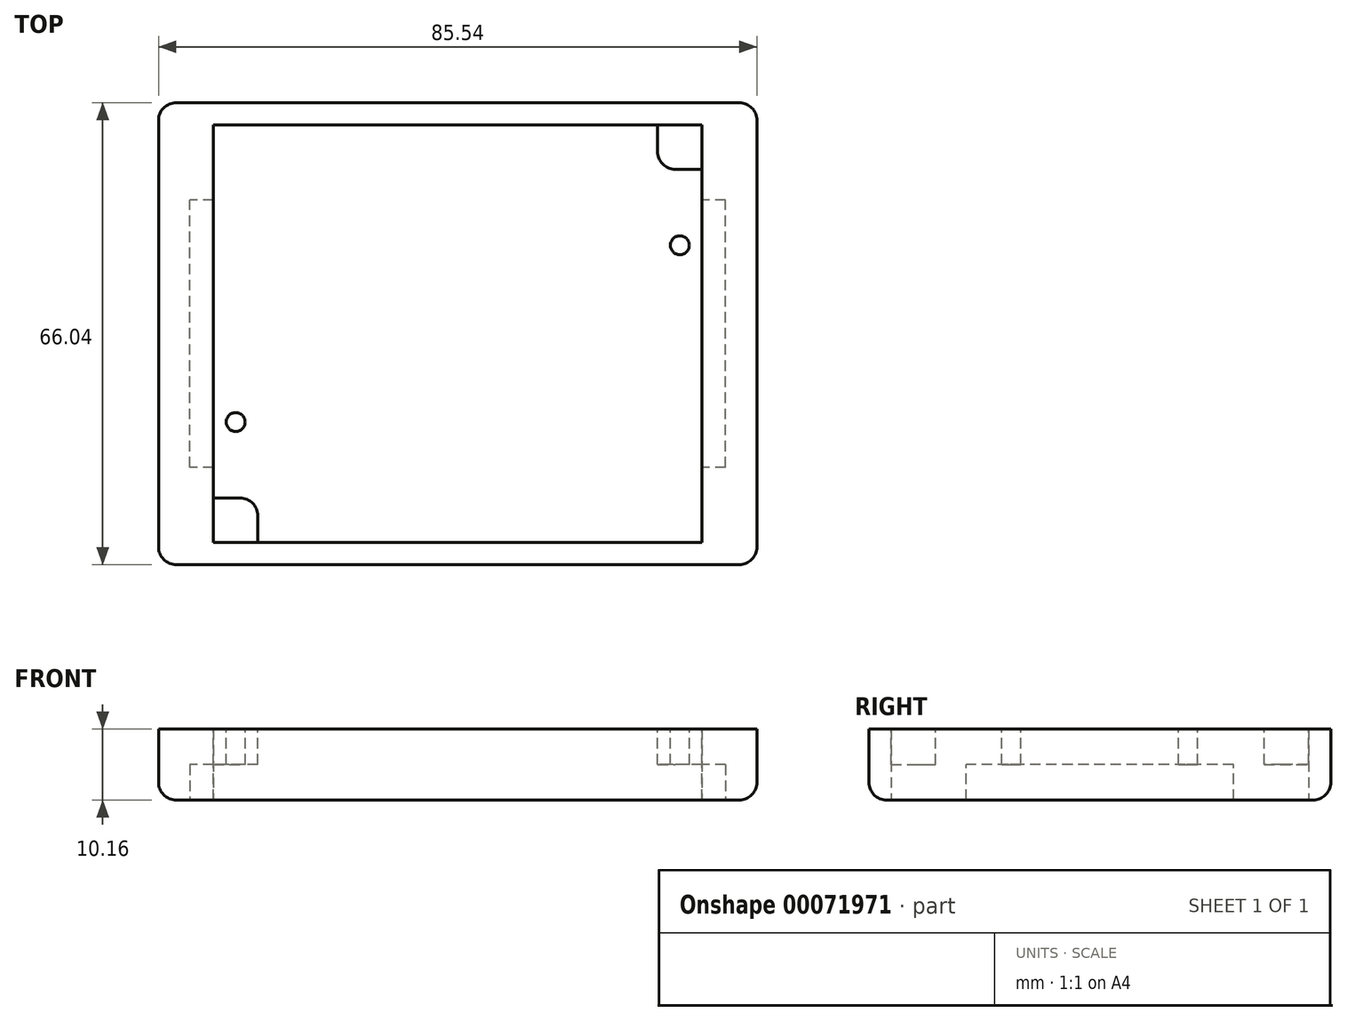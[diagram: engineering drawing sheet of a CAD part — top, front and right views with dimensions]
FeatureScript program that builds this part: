
annotation { "Feature Type Name" : "Feature", "Feature Type Description" : "" }
export const myFeature = defineFeature(function(context is Context, id is Id, definition is map)
    precondition{}
    {
        {
            var Q0;
            Q0=qCreatedBy(makeId("Top.planeOp"),FACE);
            var sketch = newSketch(context, id + "F0", { "sketchPlane" : qUnion([Q0])});
            skLineSegment(sketch, "E0.rect.bottom", {"start": v(34.92, -29.85) * mm, "end": v(-34.93, -29.85) * mm});
            skLineSegment(sketch, "E0.rect.top", {"start": v(34.92, 29.85) * mm, "end": v(-34.93, 29.85) * mm});
            skLineSegment(sketch, "E0.rect.left", {"start": v(34.92, -29.85) * mm, "end": v(34.92, 29.85) * mm});
            skLineSegment(sketch, "E0.rect.right", {"start": v(-34.93, -29.85) * mm, "end": v(-34.93, 29.85) * mm});
            skPoint(sketch, "E0.rect.middle", {"position": v(0, 0) * mm});
            skLineSegment(sketch, "E1.rect.bottom", {"start": v(42.77, -33.02) * mm, "end": v(-42.77, -33.02) * mm});
            skLineSegment(sketch, "E1.rect.top", {"start": v(42.77, 33.02) * mm, "end": v(-42.77, 33.02) * mm});
            skLineSegment(sketch, "E1.rect.left", {"start": v(42.77, -33.02) * mm, "end": v(42.77, 33.02) * mm});
            skLineSegment(sketch, "E1.rect.right", {"start": v(-42.77, -33.02) * mm, "end": v(-42.77, 33.02) * mm});
            skSolve(sketch);
        }
        {
            var Q0;
            Q0=makeQuery(id+"F0.imprint","IMPRINT",FACE,{"disambiguationData":[TD([[makeQuery(id+"F0.imprint","IMPRINT",EDGE,{"derivedFrom":sQuery(id+"F0.wireOp",EDGE,"E0.rect.bottom")}),1.0]])]});
            extrude(context, id + "F1", {"entities" : qUnion([Q0]), "depth" : 10.16 * mm});
        }
        {
            var Q0;
            Q0=makeQuery(id+"F1.opExtrude","CAP_FACE",FACE,{"disambiguationData":[OSD([sQuery(id+"F0.wireOp",EDGE,"E0.rect.bottom"),sQuery(id+"F0.wireOp",EDGE,"E0.rect.top"),sQuery(id+"F0.wireOp",EDGE,"E0.rect.left"),sQuery(id+"F0.wireOp",EDGE,"E0.rect.right"),sQuery(id+"F0.wireOp",EDGE,"E1.rect.bottom"),sQuery(id+"F0.wireOp",EDGE,"E1.rect.top"),sQuery(id+"F0.wireOp",EDGE,"E1.rect.left"),sQuery(id+"F0.wireOp",EDGE,"E1.rect.right")])],"isStart":false});
            var sketch = newSketch(context, id + "F2", { "sketchPlane" : qUnion([Q0])});
            skLineSegment(sketch, "E2.bottom", {"start": v(-34.93, -29.85) * mm, "end": v(-28.57, -29.85) * mm});
            skLineSegment(sketch, "E2.top", {"start": v(-34.93, -23.5) * mm, "end": v(-28.57, -23.5) * mm});
            skLineSegment(sketch, "E2.left", {"start": v(-34.93, -29.85) * mm, "end": v(-34.93, -23.5) * mm});
            skLineSegment(sketch, "E2.right", {"start": v(-28.57, -29.85) * mm, "end": v(-28.57, -23.5) * mm});
            skLineSegment(sketch, "E3.bottom", {"start": v(34.92, 29.85) * mm, "end": v(28.57, 29.85) * mm});
            skLineSegment(sketch, "E3.top", {"start": v(34.92, 23.5) * mm, "end": v(28.57, 23.5) * mm});
            skLineSegment(sketch, "E3.left", {"start": v(34.92, 29.85) * mm, "end": v(34.92, 23.5) * mm});
            skLineSegment(sketch, "E3.right", {"start": v(28.57, 29.85) * mm, "end": v(28.57, 23.5) * mm});
            skCircle(sketch, "E4", {"center": v(-31.75, -12.64) * mm, "radius": 1.35 * mm});
            skCircle(sketch, "E5", {"center": v(31.75, 12.64) * mm, "radius": 1.35 * mm});
            skSolve(sketch);
        }
        {
            var Q0;
            Q0 = qSketchRegion(id + "F2", true);
            extrude(context, id + "F3", {"entities" : qUnion([Q0]), "oppositeDirection" : true, "depth" : 5.08 * mm});
        }
        {
            var Q0;
            Q0=makeQuery(id+"F3.opExtrude","SWEPT_EDGE",EDGE,{"disambiguationData":[OSD([sQuery(id+"F2.wireOp",EDGE,"E3.top"),sQuery(id+"F2.wireOp",EDGE,"E3.right")])]});
            var Q1;
            Q1=makeQuery(id+"F3.opExtrude","SWEPT_EDGE",EDGE,{"disambiguationData":[OSD([sQuery(id+"F2.wireOp",EDGE,"E2.top"),sQuery(id+"F2.wireOp",EDGE,"E2.right")])]});
            fillet(context, id + "F4", {"entities" : qUnion([Q0, Q1]), "radius" : 2.54 * mm, "tangentPropagation" : true, "allowEdgeOverflow" : false});
        }
        {
            var Q0;
            Q0=makeQuery(id+"F1.opExtrude","CAP_FACE",FACE,{"disambiguationData":[OSD([sQuery(id+"F0.wireOp",EDGE,"E0.rect.bottom"),sQuery(id+"F0.wireOp",EDGE,"E0.rect.top"),sQuery(id+"F0.wireOp",EDGE,"E0.rect.left"),sQuery(id+"F0.wireOp",EDGE,"E0.rect.right"),sQuery(id+"F0.wireOp",EDGE,"E1.rect.bottom"),sQuery(id+"F0.wireOp",EDGE,"E1.rect.top"),sQuery(id+"F0.wireOp",EDGE,"E1.rect.left"),sQuery(id+"F0.wireOp",EDGE,"E1.rect.right")])],"isStart":true});
            var sketch = newSketch(context, id + "F5", { "sketchPlane" : qUnion([Q0])});
            skLineSegment(sketch, "E6.rect.bottom", {"start": v(38.3, 19.11) * mm, "end": v(-38.3, 19.11) * mm});
            skLineSegment(sketch, "E6.rect.top", {"start": v(38.3, -19.11) * mm, "end": v(-38.3, -19.11) * mm});
            skLineSegment(sketch, "E6.rect.left", {"start": v(38.3, 19.11) * mm, "end": v(38.3, -19.11) * mm});
            skLineSegment(sketch, "E6.rect.right", {"start": v(-38.3, 19.11) * mm, "end": v(-38.3, -19.11) * mm});
            skPoint(sketch, "E6.rect.middle", {"position": v(0, 0) * mm});
            skSolve(sketch);
        }
        {
            var Q0;
            Q0=makeQuery(id+"F5.imprint","IMPRINT",FACE,{"disambiguationData":[TD([[makeQuery(id+"F5.imprint","IMPRINT",EDGE,{"derivedFrom":sQuery(id+"F5.wireOp",EDGE,"E6.rect.bottom")}),1.0]])]});
            extrude(context, id + "F6", {"entities" : qUnion([Q0]), "operationType" : NewBodyOperationType.REMOVE, "oppositeDirection" : true, "depth" : 5.08 * mm});
        }
        {
            var Q0;
            Q0=makeQuery(id+"F1.opExtrude","SWEPT_EDGE",EDGE,{"disambiguationData":[OSD([sQuery(id+"F0.wireOp",EDGE,"E1.rect.bottom"),sQuery(id+"F0.wireOp",EDGE,"E1.rect.left")])]});
            var Q1;
            Q1=makeQuery(id+"F1.opExtrude","SWEPT_EDGE",EDGE,{"disambiguationData":[OSD([sQuery(id+"F0.wireOp",EDGE,"E1.rect.top"),sQuery(id+"F0.wireOp",EDGE,"E1.rect.left")])]});
            var Q2;
            Q2=makeQuery(id+"F1.opExtrude","SWEPT_EDGE",EDGE,{"disambiguationData":[OSD([sQuery(id+"F0.wireOp",EDGE,"E1.rect.bottom"),sQuery(id+"F0.wireOp",EDGE,"E1.rect.right")])]});
            var Q3;
            Q3=makeQuery(id+"F1.opExtrude","SWEPT_EDGE",EDGE,{"disambiguationData":[OSD([sQuery(id+"F0.wireOp",EDGE,"E1.rect.top"),sQuery(id+"F0.wireOp",EDGE,"E1.rect.right")])]});
            var Q4;
            Q4=makeQuery(id+"F1.opExtrude","CAP_EDGE",EDGE,{"disambiguationData":[OSD([sQuery(id+"F0.wireOp",EDGE,"E1.rect.bottom")])],"isStart":true});
            var Q5;
            Q5=makeQuery(id+"F1.opExtrude","CAP_EDGE",EDGE,{"disambiguationData":[OSD([sQuery(id+"F0.wireOp",EDGE,"E1.rect.left")])],"isStart":true});
            var Q6;
            Q6=makeQuery(id+"F1.opExtrude","CAP_EDGE",EDGE,{"disambiguationData":[OSD([sQuery(id+"F0.wireOp",EDGE,"E1.rect.top")])],"isStart":true});
            var Q7;
            Q7=makeQuery(id+"F1.opExtrude","CAP_EDGE",EDGE,{"disambiguationData":[OSD([sQuery(id+"F0.wireOp",EDGE,"E1.rect.right")])],"isStart":true});
            fillet(context, id + "F7", {"entities" : qUnion([Q0, Q1, Q2, Q3, Q4, Q5, Q6, Q7]), "radius" : 2.54 * mm, "tangentPropagation" : true, "allowEdgeOverflow" : false});
        }
    });
